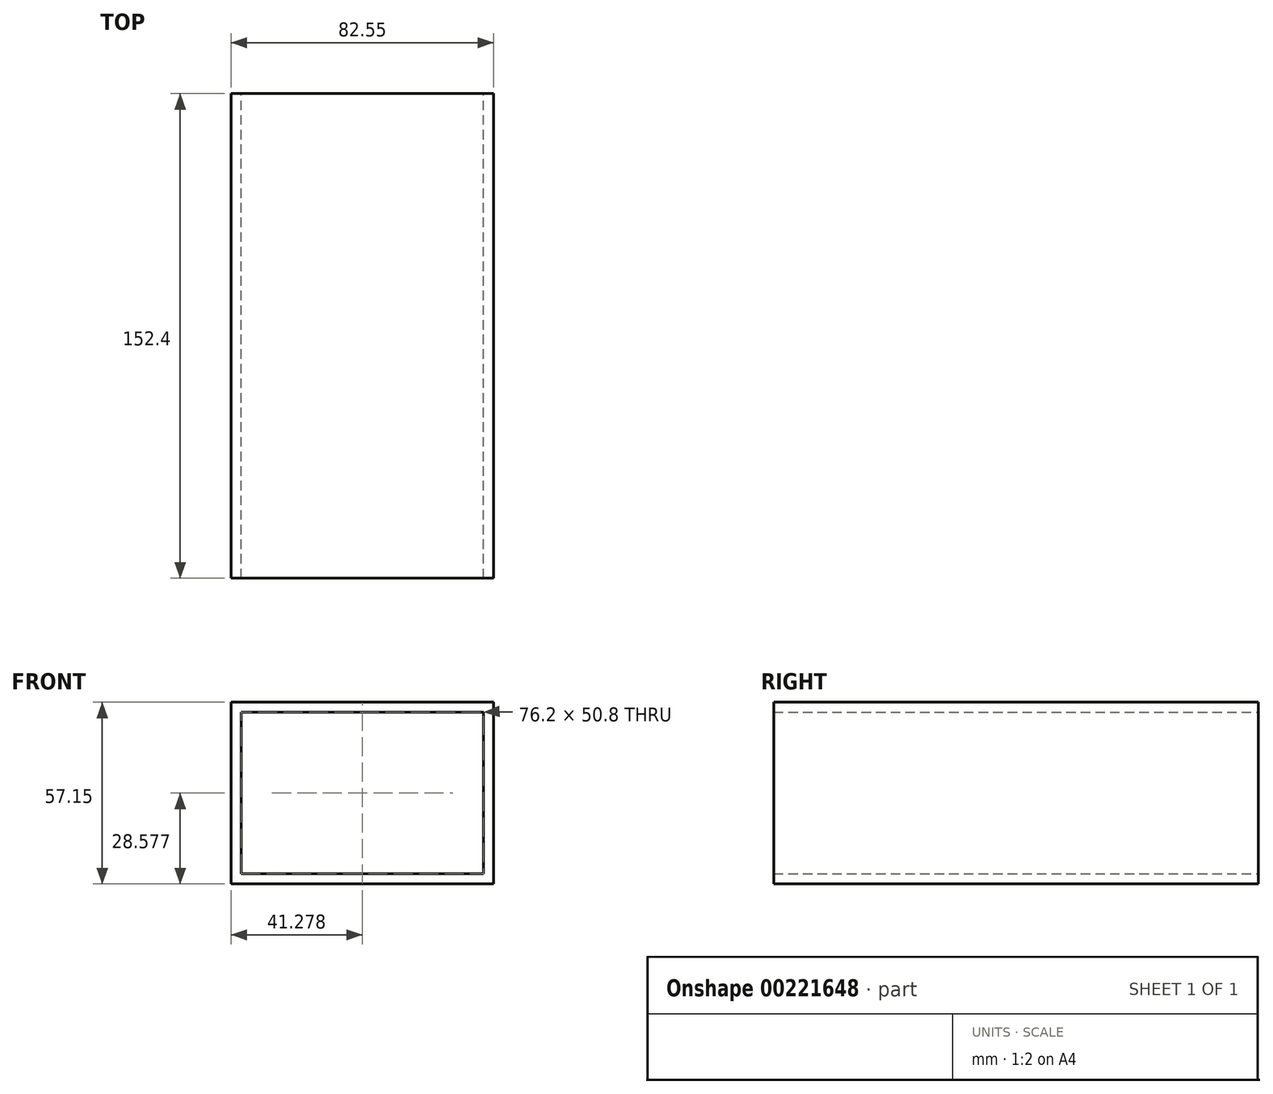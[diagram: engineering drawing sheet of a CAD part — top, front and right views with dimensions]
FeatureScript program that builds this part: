
annotation { "Feature Type Name" : "Feature", "Feature Type Description" : "" }
export const myFeature = defineFeature(function(context is Context, id is Id, definition is map)
    precondition{}
    {
        {
            var Q0;
            Q0=qCreatedBy(makeId("Front.planeOp"),FACE);
            var sketch = newSketch(context, id + "F0", { "sketchPlane" : qUnion([Q0])});
            skLineSegment(sketch, "E0.bottom", {"start": v(-34.37, 6.03) * mm, "end": v(41.83, 6.03) * mm});
            skLineSegment(sketch, "E0.top", {"start": v(-34.37, -44.77) * mm, "end": v(41.83, -44.77) * mm});
            skLineSegment(sketch, "E0.left", {"start": v(-34.37, 6.03) * mm, "end": v(-34.37, -44.77) * mm});
            skLineSegment(sketch, "E0.right", {"start": v(41.83, 6.03) * mm, "end": v(41.83, -44.77) * mm});
            skLineSegment(sketch, "E1.0", {"start": v(-37.55, 9.2) * mm, "end": v(45, 9.2) * mm});
            skLineSegment(sketch, "E1.1", {"start": v(-37.55, 9.2) * mm, "end": v(-37.55, -47.95) * mm});
            skLineSegment(sketch, "E1.2", {"start": v(-37.55, -47.95) * mm, "end": v(45, -47.95) * mm});
            skLineSegment(sketch, "E1.3", {"start": v(45, 9.2) * mm, "end": v(45, -47.95) * mm});
            skSolve(sketch);
        }
        {
            var Q0;
            Q0=makeQuery(id+"F0.imprint","IMPRINT",FACE,{"disambiguationData":[TD([[makeQuery(id+"F0.imprint","IMPRINT",EDGE,{"derivedFrom":sQuery(id+"F0.wireOp",EDGE,"E0.bottom")}),1.0]])]});
            extrude(context, id + "F1", {"entities" : qUnion([Q0]), "depth" : 152.4 * mm});
        }
    });
